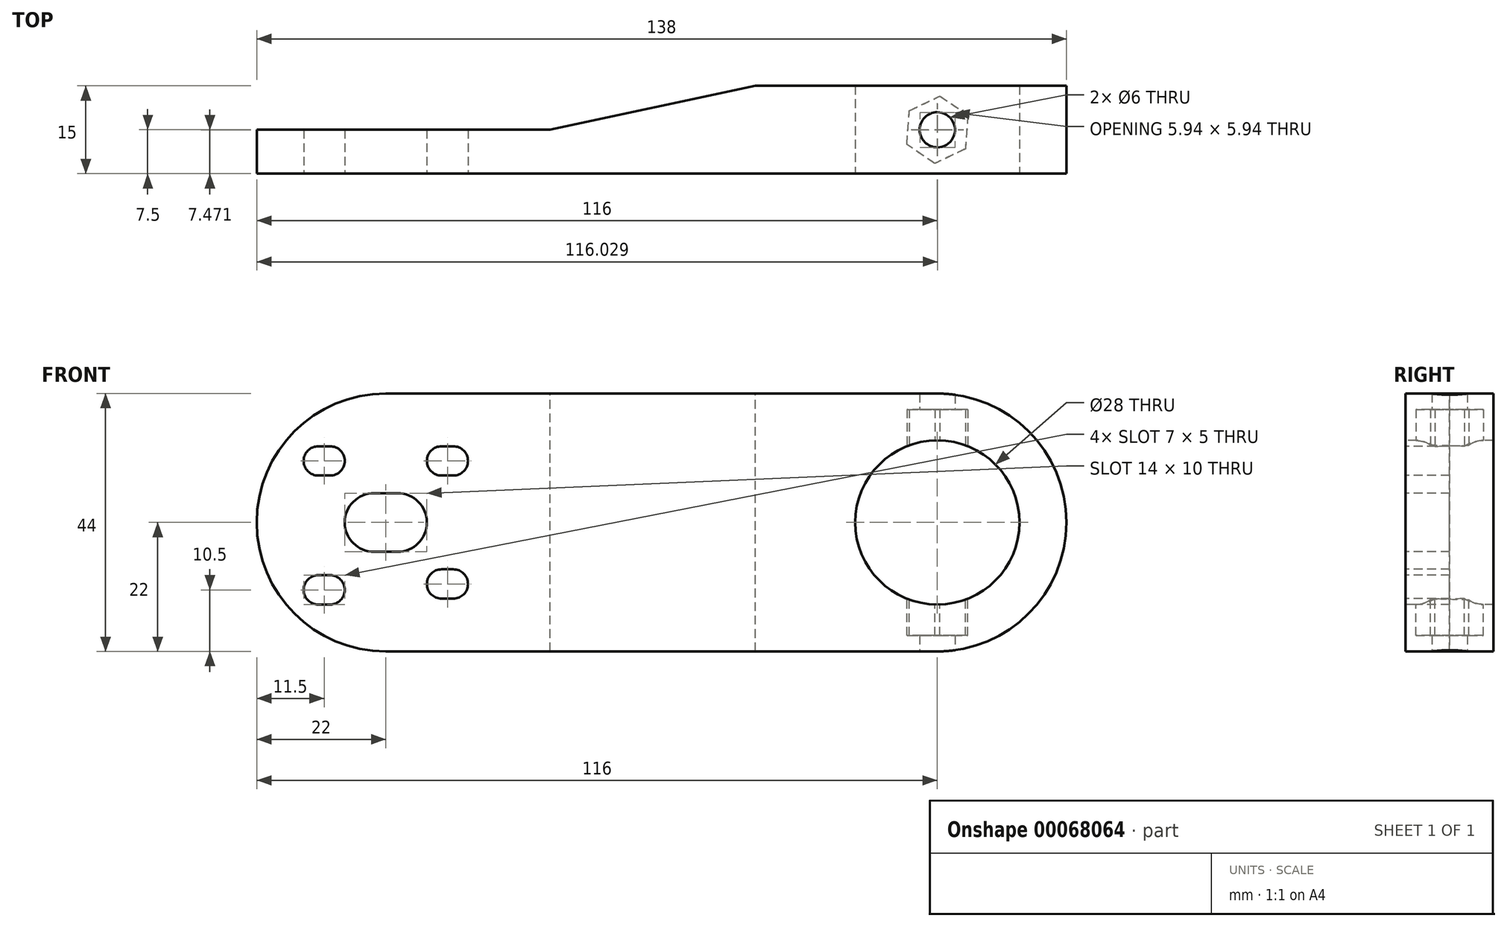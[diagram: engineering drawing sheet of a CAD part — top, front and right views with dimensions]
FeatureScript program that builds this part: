
annotation { "Feature Type Name" : "Feature", "Feature Type Description" : "" }
export const myFeature = defineFeature(function(context is Context, id is Id, definition is map)
    precondition{}
    {
        {
            var Q0;
            Q0=qCreatedBy(makeId("Front.planeOp"),FACE);
            var sketch = newSketch(context, id + "F0", { "sketchPlane" : qUnion([Q0])});
            skArc(sketch, "E0", {"start": v(-94, 44) * mm, "mid": v(-116, 22) * mm, "end": v(-94, 0) * mm});
            skArc(sketch, "E1", {"start": v(0, 0) * mm, "mid": v(22, 22) * mm, "end": v(0, 44) * mm});
            skLineSegment(sketch, "E2", {"start": v(-94, 44) * mm, "end": v(0, 44) * mm});
            skLineSegment(sketch, "E3", {"start": v(0, 0) * mm, "end": v(-94, 0) * mm});
            skCircle(sketch, "E4", {"center": v(0, 22) * mm, "radius": 14 * mm});
            skLineSegment(sketch, "E5.rect.bottom", {"start": v(-92, 27) * mm, "end": v(-96, 27) * mm});
            skLineSegment(sketch, "E5.rect.top", {"start": v(-92, 17) * mm, "end": v(-96, 17) * mm});
            skArc(sketch, "E6", {"start": v(-96, 27) * mm, "mid": v(-101, 22) * mm, "end": v(-96, 17) * mm});
            skArc(sketch, "E7", {"start": v(-92, 17) * mm, "mid": v(-87, 22) * mm, "end": v(-92, 27) * mm});
            skPoint(sketch, "E8.rect.middle", {"position": v(-83.5, 11.5) * mm});
            skLineSegment(sketch, "E9.rect.bottom", {"start": v(-82.5, 14) * mm, "end": v(-84.5, 14) * mm});
            skLineSegment(sketch, "E9.rect.top", {"start": v(-82.5, 9) * mm, "end": v(-84.5, 9) * mm});
            skArc(sketch, "E10", {"start": v(-84.5, 14) * mm, "mid": v(-87, 11.5) * mm, "end": v(-84.5, 9) * mm});
            skArc(sketch, "E11", {"start": v(-82.5, 9) * mm, "mid": v(-80, 11.5) * mm, "end": v(-82.5, 14) * mm});
            skLineSegment(sketch, "E12.rect.bottom", {"start": v(-82.5, 35) * mm, "end": v(-84.5, 35) * mm});
            skLineSegment(sketch, "E12.rect.top", {"start": v(-82.5, 30) * mm, "end": v(-84.5, 30) * mm});
            skPoint(sketch, "E12.rect.middle", {"position": v(-83.5, 32.5) * mm});
            skLineSegment(sketch, "E13.rect.bottom", {"start": v(-103.5, 35) * mm, "end": v(-105.5, 35) * mm});
            skLineSegment(sketch, "E13.rect.top", {"start": v(-103.5, 30) * mm, "end": v(-105.5, 30) * mm});
            skPoint(sketch, "E13.rect.middle", {"position": v(-104.5, 32.5) * mm});
            skLineSegment(sketch, "E14.rect.bottom", {"start": v(-103.5, 13) * mm, "end": v(-105.5, 13) * mm});
            skLineSegment(sketch, "E14.rect.top", {"start": v(-103.5, 8) * mm, "end": v(-105.5, 8) * mm});
            skPoint(sketch, "E14.rect.middle", {"position": v(-104.5, 10.5) * mm});
            skArc(sketch, "E15", {"start": v(-105.5, 35) * mm, "mid": v(-108, 32.5) * mm, "end": v(-105.5, 30) * mm});
            skArc(sketch, "E16", {"start": v(-103.5, 30) * mm, "mid": v(-101, 32.5) * mm, "end": v(-103.5, 35) * mm});
            skArc(sketch, "E17", {"start": v(-84.5, 35) * mm, "mid": v(-87, 32.5) * mm, "end": v(-84.5, 30) * mm});
            skArc(sketch, "E18", {"start": v(-82.5, 30) * mm, "mid": v(-80, 32.5) * mm, "end": v(-82.5, 35) * mm});
            skArc(sketch, "E19", {"start": v(-103.5, 8) * mm, "mid": v(-101, 10.5) * mm, "end": v(-103.5, 13) * mm});
            skArc(sketch, "E20", {"start": v(-105.5, 13) * mm, "mid": v(-108, 10.5) * mm, "end": v(-105.5, 8) * mm});
            skSolve(sketch);
        }
        {
            var Q0;
            Q0=makeQuery(id+"F0.imprint","IMPRINT",FACE,{"disambiguationData":[TD([[makeQuery(id+"F0.imprint","IMPRINT",EDGE,{"derivedFrom":sQuery(id+"F0.wireOp",EDGE,"E0")}),1.0]])]});
            extrude(context, id + "F1", {"entities" : qUnion([Q0]), "oppositeDirection" : true, "depth" : 15 * mm});
        }
        {
            var Q0;
            Q0=qCreatedBy(makeId("Top.planeOp"),FACE);
            var sketch = newSketch(context, id + "F2", { "sketchPlane" : qUnion([Q0])});
            skCircle(sketch, "E21", {"center": v(0, 7.5) * mm, "radius": 3 * mm});
            skSolve(sketch);
        }
        {
            var Q0;
            Q0=makeQuery(id+"F2.imprint","IMPRINT",FACE,{"disambiguationData":[TD([[makeQuery(id+"F2.imprint","IMPRINT",EDGE,{"derivedFrom":sQuery(id+"F2.wireOp",EDGE,"E21")}),1.0]])]});
            extrude(context, id + "F3", {"entities" : qUnion([Q0]), "operationType" : NewBodyOperationType.REMOVE, "depth" : 50 * mm});
        }
        {
            var Q0;
            Q0=qCreatedBy(makeId("Top.planeOp"),FACE);
            cPlane(context, id + "F4", {"entities" : qUnion([Q0]), "cplaneType" : CPlaneType.OFFSET, "offset" : 22 * mm, "width" : 150 * mm, "height" : 150 * mm});
        }
        {
            var Q0;
            Q0=qCreatedBy(id+"F4.planeOp",FACE);
            var sketch = newSketch(context, id + "F5", { "sketchPlane" : qUnion([Q0])});
            skCircle(sketch, "E22.cCircle", {"center": v(0, 7.5) * mm, "radius": 5 * mm, "construction": true});
            skLineSegment(sketch, "E22.0", {"start": v(5.2, 10) * mm, "end": v(4.77, 4.24) * mm});
            skLineSegment(sketch, "E22.1", {"start": v(4.77, 4.24) * mm, "end": v(-0.44, 1.74) * mm});
            skLineSegment(sketch, "E22.2", {"start": v(-0.44, 1.74) * mm, "end": v(-5.2, 5) * mm});
            skLineSegment(sketch, "E22.3", {"start": v(-5.2, 5) * mm, "end": v(-4.77, 10.76) * mm});
            skLineSegment(sketch, "E22.4", {"start": v(-4.77, 10.76) * mm, "end": v(0.44, 13.26) * mm});
            skLineSegment(sketch, "E22.5", {"start": v(0.44, 13.26) * mm, "end": v(5.2, 10) * mm});
            skPoint(sketch, "E22.0.midPoint", {"position": v(4.99, 7.12) * mm});
            skSolve(sketch);
        }
        {
            var Q0;
            Q0=makeQuery(id+"F5.imprint","IMPRINT",FACE,{"disambiguationData":[TD([[makeQuery(id+"F5.imprint","IMPRINT",EDGE,{"derivedFrom":sQuery(id+"F5.wireOp",EDGE,"E22.0")}),-1.0]])]});
            extrude(context, id + "F6", {"entities" : qUnion([Q0]), "operationType" : NewBodyOperationType.REMOVE, "depth" : 19.3 * mm});
        }
        {
            var Q0;
            Q0 = qSketchRegion(id + "F5", true);
            extrude(context, id + "F7", {"entities" : qUnion([Q0]), "operationType" : NewBodyOperationType.REMOVE, "oppositeDirection" : true, "depth" : 19.3 * mm});
        }
        {
            var Q0;
            Q0=qCreatedBy(id+"F4.planeOp",FACE);
            var sketch = newSketch(context, id + "F8", { "sketchPlane" : qUnion([Q0])});
            skLineSegment(sketch, "E23", {"start": v(-116, 7.5) * mm, "end": v(-66, 7.5) * mm});
            skLineSegment(sketch, "E24", {"start": v(-66, 7.5) * mm, "end": v(-31, 15) * mm});
            skLineSegment(sketch, "E25", {"start": v(-31, 15) * mm, "end": v(-116, 15) * mm});
            skLineSegment(sketch, "E26", {"start": v(-116, 15) * mm, "end": v(-116, 7.5) * mm});
            skSolve(sketch);
        }
        {
            var Q0;
            Q0 = qSketchRegion(id + "F8", true);
            extrude(context, id + "F9", {"entities" : qUnion([Q0]), "operationType" : NewBodyOperationType.REMOVE, "oppositeDirection" : true, "depth" : 25 * mm});
        }
        {
            var Q0;
            Q0 = qSketchRegion(id + "F8", true);
            extrude(context, id + "F10", {"entities" : qUnion([Q0]), "operationType" : NewBodyOperationType.REMOVE, "depth" : 25 * mm});
        }
    });
